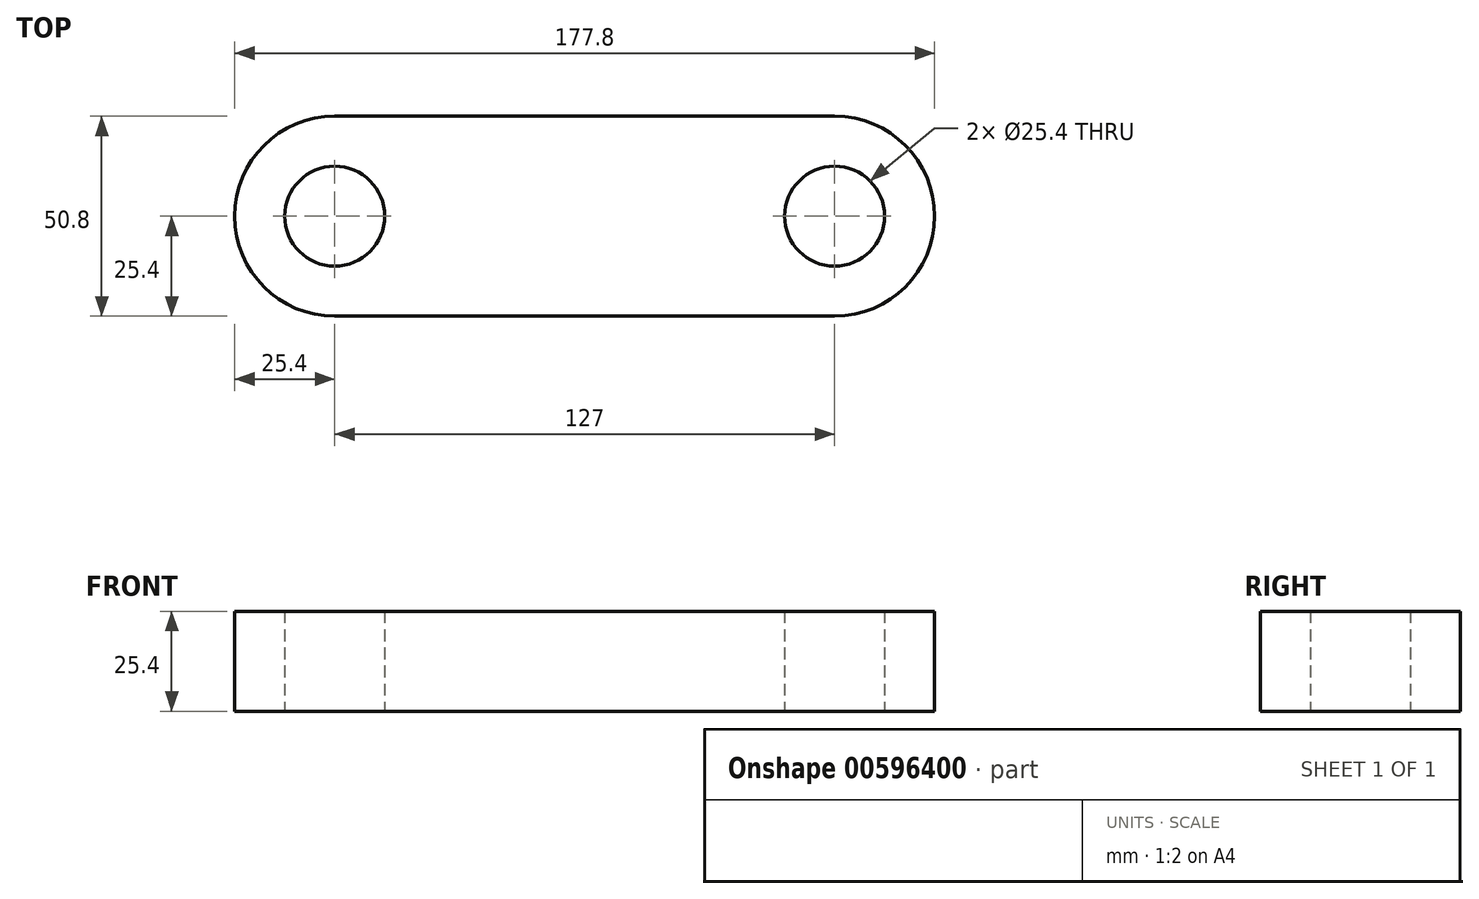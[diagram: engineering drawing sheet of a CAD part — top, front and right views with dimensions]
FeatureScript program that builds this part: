
annotation { "Feature Type Name" : "Feature", "Feature Type Description" : "" }
export const myFeature = defineFeature(function(context is Context, id is Id, definition is map)
    precondition{}
    {
        {
            var Q0;
            Q0=qCreatedBy(makeId("Top.planeOp"),FACE);
            var sketch = newSketch(context, id + "F0", { "sketchPlane" : qUnion([Q0])});
            skLineSegment(sketch, "E0", {"start": v(0, 50.8) * mm, "end": v(-127, 50.8) * mm});
            skLineSegment(sketch, "E1", {"start": v(-127, 0) * mm, "end": v(0, 0) * mm});
            skArc(sketch, "E2", {"start": v(-127, 50.8) * mm, "mid": v(-152.4, 25.4) * mm, "end": v(-127, 0) * mm});
            skPoint(sketch, "E3.center.orphan", {"position": v(0, 25.4) * mm});
            skArc(sketch, "E4", {"start": v(0, 50.8) * mm, "mid": v(25.4, 25.4) * mm, "end": v(0, 0) * mm});
            skCircle(sketch, "E5", {"center": v(-127, 25.4) * mm, "radius": 12.7 * mm});
            skCircle(sketch, "E6", {"center": v(0, 25.4) * mm, "radius": 179044.6 * mm});
            skCircle(sketch, "E7", {"center": v(0, 25.4) * mm, "radius": 12.7 * mm});
            skSolve(sketch);
        }
        {
            var Q0;
            Q0=makeQuery(id+"F0.imprint","IMPRINT",FACE,{"disambiguationData":[TD([[makeQuery(id+"F0.imprint","IMPRINT",EDGE,{"derivedFrom":sQuery(id+"F0.wireOp",EDGE,"E0")}),1.0]])]});
            extrude(context, id + "F1", {"entities" : qUnion([Q0]), "depth" : 25.4 * mm, "offsetDistance" : 25.4 * mm});
        }
    });
